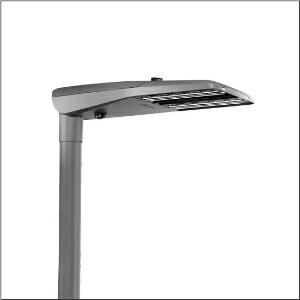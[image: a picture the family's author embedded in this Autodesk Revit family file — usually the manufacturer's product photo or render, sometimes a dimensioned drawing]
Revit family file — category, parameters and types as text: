
# Revit family: streetlight_sl_11_iq_midi___st1_2a_5xc3a51y08me_2b41
name_source: partatom
category: Lighting Fixtures
units: mm (PartAtom-declared; Revit-internal decimal feet)

## family parameters
Cut with Voids When Loaded = No
Host = Face
Light Source = No
Part Type = Normal
Room Calculation Point = No
Round Connector Dimension = Use Diameter
Shared = No

## types (1)
- --- (1 x LED, 18110 lm, 122.7 W, 3000K)
    Apparent Load = 123 VA
    CIE Flux Codes = 32 70 96 100 100
    Color Rendering = 70
    Color Temperature = 3000K
    Default Elevation = 1800 mm
    Description = Streetlight SL 11 iQ midi, mast luminaire, primary light control with 3 zone facetted reflector, of plastic, silver coated, highly specular, primary optical cover: cover, of PMMA, transparent, light distribution: ST1.2a, light emission: direct distribution, primary light characteristic: asymmetric, installation type: post-top, side-entry, LED, High Power LED, rated luminous flux: 18.110lm, luminous efficacy: 148lm/W, light colour: 730, colour temperature: 3000K, control: pre-setting: logarithmic dimming characteristic, Street-Remote, Auto-Match, Temp-Guard, Lumen-Switch, Night-Set, Smart-Wire, Light-Fading, Desk-Remote (wireless, voltage-free reading and setting of iQ features in the workshop via application-optimized NFC function/RFID function), optimised constant luminous flux control (CLO 2.0), with cable H07RN-F 5x 1.5mm², mains connection: 230..240V, AC, 50/60Hz, connection cable pre-assembled, cable length: 12,5m, start of lifetime: 123W, end of service life: 130W, reduction: 56W, luminaire housing, of diecast aluminium, powder-coated, Siteco® metallic grey (DB 702S), please order mast flange separately, inclination adjustable without tools: 0°, 5°, 10°, 15° (post-top) | 0°, -5°, -10°, -15° (side-entry), sealing non-destructively replaceable, multi-level sealing system, length: 780mm, width: 376mm, height: 118mm, mast flange for spigot size: 42mm (side-entry): 5XC10008XM4, 60/48mm (side-entry/post-top): 5XC10108XM2, 76/60mm (side-entry/post-top): 5XC10108XM1, equipment: Power, Smart Interface below and above, protection rating (complete): IP66, insulation class (complete): insulation class II (safety insulation), certification: CE, ENEC, VDE, UKCA, impact resistance: IK09, permissible operating ambient temperature for outdoor applications: -25..+50°C, standard-compliant lighting for roads and squares, Environmental Product Declaration (EPD) tested and certified by an independent institute, packaging unit: 1 piece

Light Distribution: ST1.2a
    Height = 118 mm
    Lamp = 1 x LED
    Lamp Light Flux = 18110 lm
    Lamp Power = 122.7 W
    Lamp count = 1
    Length = 780 mm
    Luminous efficacy = 148 lm/W
    Manufacturer = Siteco
    ModVariant = No
    Model = 5XC3A51Y08ME
    Number of Poles = 1
    OnlyDefault = Yes
    Power Factor = 1
    Product Name = Streetlight SL 11 iQ midi | ST1.2a
    Product group = mast luminaire | pylon top
    ProductGroupID = 6100
    Protection Class = Protection class II
    Protection Degree = IP 66
    RLX_Detail_Level = 1
    RLX_Emergency_Light_Flux = 0 lm
    RLX_Emergency_Type = 0
    RLX_Emergency_Type_DB = No
    RlxData = <blob elided: 69857 chars, md5=10425022>
    Socket = socket
    Standby Power = 0 W
    System Light Flux = 18111 lm
    System Power = 123 W
    Type Comments = factory setting: luminous flux: 100 % | dim-lin: 254 | 553 mA
    Type Image = l_1004429.jpg
    URL = http://relux.com
    VarID = @adj_103069
    Voltage = 0 V
    Weight = 0.00 kg
    Width = 376 mm

## geometry (parser evidence)
native form markers: Blend x4, Sweep x9
no freeform markers — native parametric forms only
